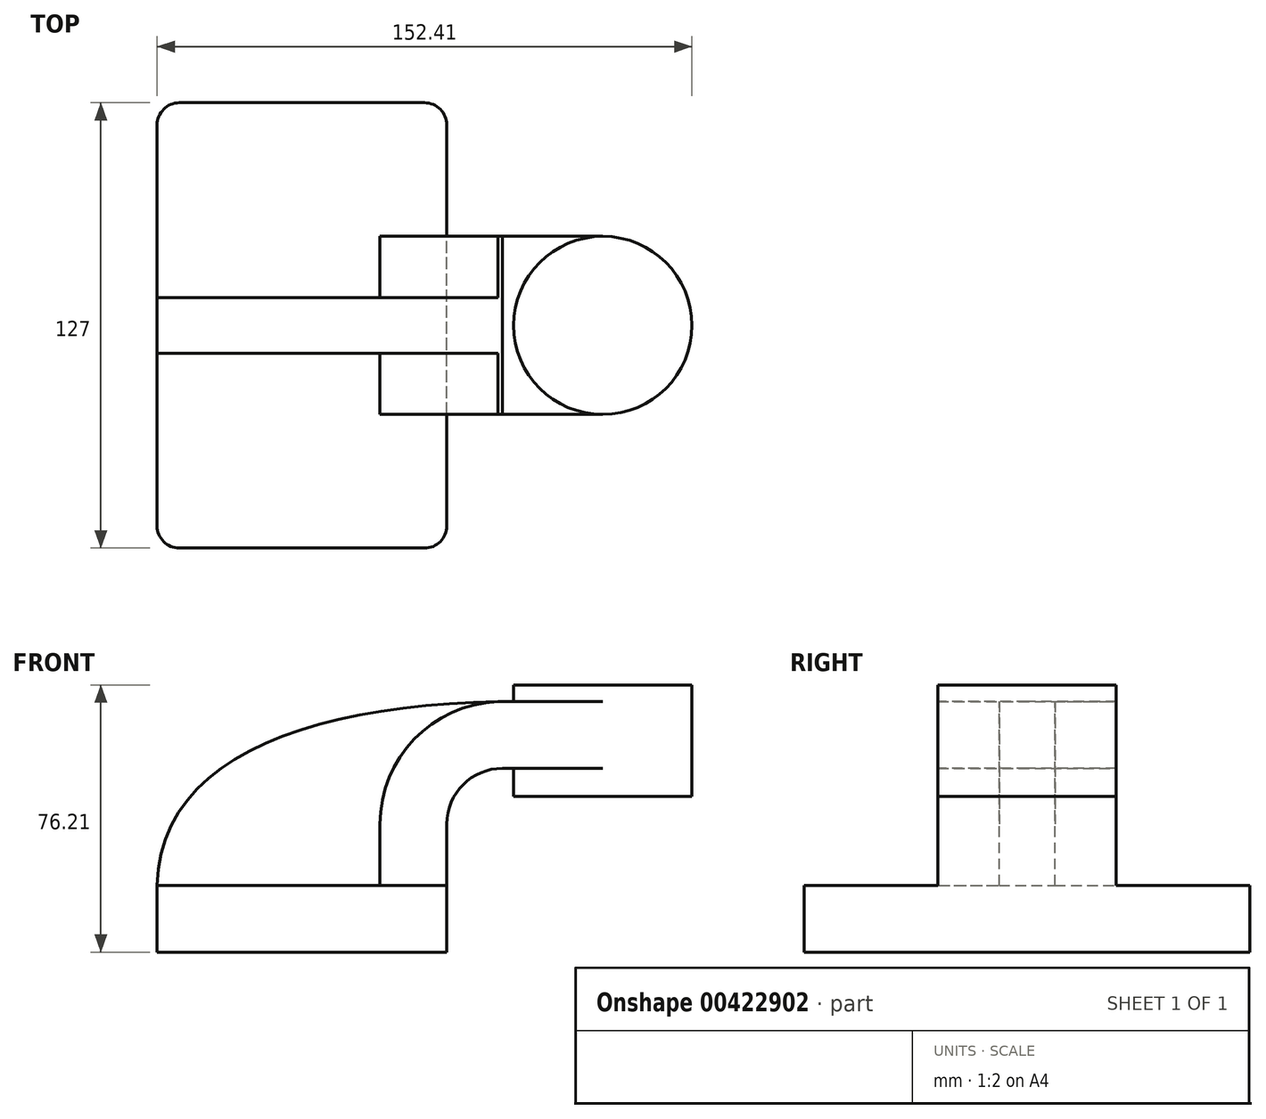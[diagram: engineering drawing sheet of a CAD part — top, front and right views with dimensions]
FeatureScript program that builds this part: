
annotation { "Feature Type Name" : "Feature", "Feature Type Description" : "" }
export const myFeature = defineFeature(function(context is Context, id is Id, definition is map)
    precondition{}
    {
        {
            var Q0;
            Q0=qCreatedBy(makeId("Front.planeOp"),FACE);
            var sketch = newSketch(context, id + "F0", { "sketchPlane" : qUnion([Q0])});
            skLineSegment(sketch, "E0.bottom", {"start": v(-41.28, 9.53) * mm, "end": v(41.28, 9.53) * mm});
            skLineSegment(sketch, "E0.top", {"start": v(-41.28, -9.53) * mm, "end": v(41.28, -9.53) * mm});
            skLineSegment(sketch, "E0.left", {"start": v(-41.28, 9.53) * mm, "end": v(-41.28, -9.53) * mm});
            skLineSegment(sketch, "E0.right", {"start": v(41.28, 9.53) * mm, "end": v(41.28, -9.53) * mm});
            skPoint(sketch, "E0.middle", {"position": v(0, 0) * mm});
            skLineSegment(sketch, "E1.bottom", {"start": v(111.13, 34.93) * mm, "end": v(60.33, 34.93) * mm});
            skLineSegment(sketch, "E1.top", {"start": v(111.13, 66.68) * mm, "end": v(60.33, 66.68) * mm});
            skLineSegment(sketch, "E1.left", {"start": v(111.13, 34.93) * mm, "end": v(111.13, 66.68) * mm});
            skLineSegment(sketch, "E1.right", {"start": v(60.33, 34.93) * mm, "end": v(60.33, 66.67) * mm});
            skPoint(sketch, "E1.middle", {"position": v(85.73, 50.8) * mm});
            skLineSegment(sketch, "E2", {"start": v(41.28, 9.53) * mm, "end": v(41.28, 27) * mm});
            skArc(sketch, "E3", {"start": v(41.28, 27) * mm, "mid": v(45.92, 38.23) * mm, "end": v(57.15, 42.88) * mm});
            skLineSegment(sketch, "E4", {"start": v(57.15, 42.88) * mm, "end": v(85.73, 42.88) * mm});
            skPoint(sketch, "E4.endSnap0", {"position": v(85.73, 34.93) * mm});
            skLineSegment(sketch, "E5.0", {"start": v(57.15, 61.93) * mm, "end": v(85.73, 61.93) * mm});
            skArc(sketch, "E5.1", {"start": v(22.23, 27) * mm, "mid": v(32.45, 51.7) * mm, "end": v(57.15, 61.93) * mm});
            skLineSegment(sketch, "E5.2", {"start": v(22.23, 9.53) * mm, "end": v(22.23, 27) * mm});
            skLineSegment(sketch, "E6", {"start": v(85.73, 34.93) * mm, "end": v(85.73, 66.68) * mm});
            skFitSpline(sketch, "E7", {"points": [v(-41.28, 9.53) * mm, v(57.15, 61.93) * mm], "startDerivative": vector(2.55, 110.3) * mm, "endDerivative": vector(164.16, 2.84) * mm});
            skSolve(sketch);
        }
        {
            var Q0;
            Q0=makeQuery(id+"F0.imprint","IMPRINT",FACE,{"disambiguationData":[TD([[makeQuery(id+"F0.imprint","IMPRINT",EDGE,{"derivedFrom":sQuery(id+"F0.wireOp",EDGE,"E0.top")}),1.0]])]});
            extrude(context, id + "F1", {"entities" : qUnion([Q0]), "endBound" : BoundingType.SYMMETRIC, "depth" : 127 * mm});
        }
        {
            var Q0;
            {var subQ1=sQuery(id+"F0.wireOp",EDGE,"E2");Q0=makeQuery(id+"F0.imprint","IMPRINT",FACE,{"disambiguationData":[TD([[makeQuery(id+"F0.imprint","IMPRINT",EDGE,{"derivedFrom":subQ1}),1.0]])]});}
            var Q1;
            {var subQ0=sQuery(id+"F0.wireOp",EDGE,"E4");var subQ1=sQuery(id+"F0.wireOp",EDGE,"E1.right");var subQ2=makeQuery(id+"F0.imprint","INTERSECT",VERTEX,{"derivedFrom":[subQ1,subQ0]});Q1=makeQuery(id+"F0.imprint","IMPRINT",FACE,{"disambiguationData":[TD([[makeQuery(id+"F0.imprint","IMPRINT",EDGE,{"disambiguationData":[TD([[subQ2,-1.0]])],"derivedFrom":subQ1}),-1.0]])]});}
            extrude(context, id + "F2", {"entities" : qUnion([Q0, Q1]), "operationType" : NewBodyOperationType.ADD, "endBound" : BoundingType.SYMMETRIC, "depth" : 50.8 * mm});
        }
        {
            var Q0;
            {var subQ3=sQuery(id+"F0.wireOp",EDGE,"E5.2");Q0=makeQuery(id+"F0.imprint","IMPRINT",FACE,{"disambiguationData":[TD([[makeQuery(id+"F0.imprint","IMPRINT",EDGE,{"derivedFrom":subQ3}),1.0]])]});}
            extrude(context, id + "F3", {"entities" : qUnion([Q0]), "operationType" : NewBodyOperationType.ADD, "endBound" : BoundingType.SYMMETRIC, "depth" : 15.88 * mm});
        }
        {
            var Q0;
            {var subQ0=sQuery(id+"F0.wireOp",EDGE,"E1.left");Q0=makeQuery(id+"F0.imprint","IMPRINT",FACE,{"disambiguationData":[TD([[makeQuery(id+"F0.imprint","IMPRINT",EDGE,{"derivedFrom":subQ0}),1.0]])]});}
            var Q1;
            Q1=sQuery(id+"F0.wireOp",EDGE,"E6");
            revolve(context, id + "F4", {"operationType" : NewBodyOperationType.ADD, "entities" : qUnion([Q0]), "axis" : qUnion([Q1]), "revolveType" : RevolveType.FULL});
        }
        {
            var Q0;
            Q0=makeQuery(id+"F1.opExtrude","CAP_EDGE",EDGE,{"disambiguationData":[OSD([sQuery(id+"F0.wireOp",EDGE,"E0.right")])],"isStart":false});
            var Q1;
            Q1=makeQuery(id+"F1.opExtrude","CAP_EDGE",EDGE,{"disambiguationData":[OSD([sQuery(id+"F0.wireOp",EDGE,"E0.left")])],"isStart":false});
            var Q2;
            Q2=makeQuery(id+"F1.opExtrude","CAP_EDGE",EDGE,{"disambiguationData":[OSD([sQuery(id+"F0.wireOp",EDGE,"E0.left")])],"isStart":true});
            var Q3;
            Q3=makeQuery(id+"F1.opExtrude","CAP_EDGE",EDGE,{"disambiguationData":[OSD([sQuery(id+"F0.wireOp",EDGE,"E0.right")])],"isStart":true});
            fillet(context, id + "F5", {"entities" : qUnion([Q0, Q1, Q2, Q3]), "radius" : 6.35 * mm, "tangentPropagation" : true, "allowEdgeOverflow" : false});
        }
    });
